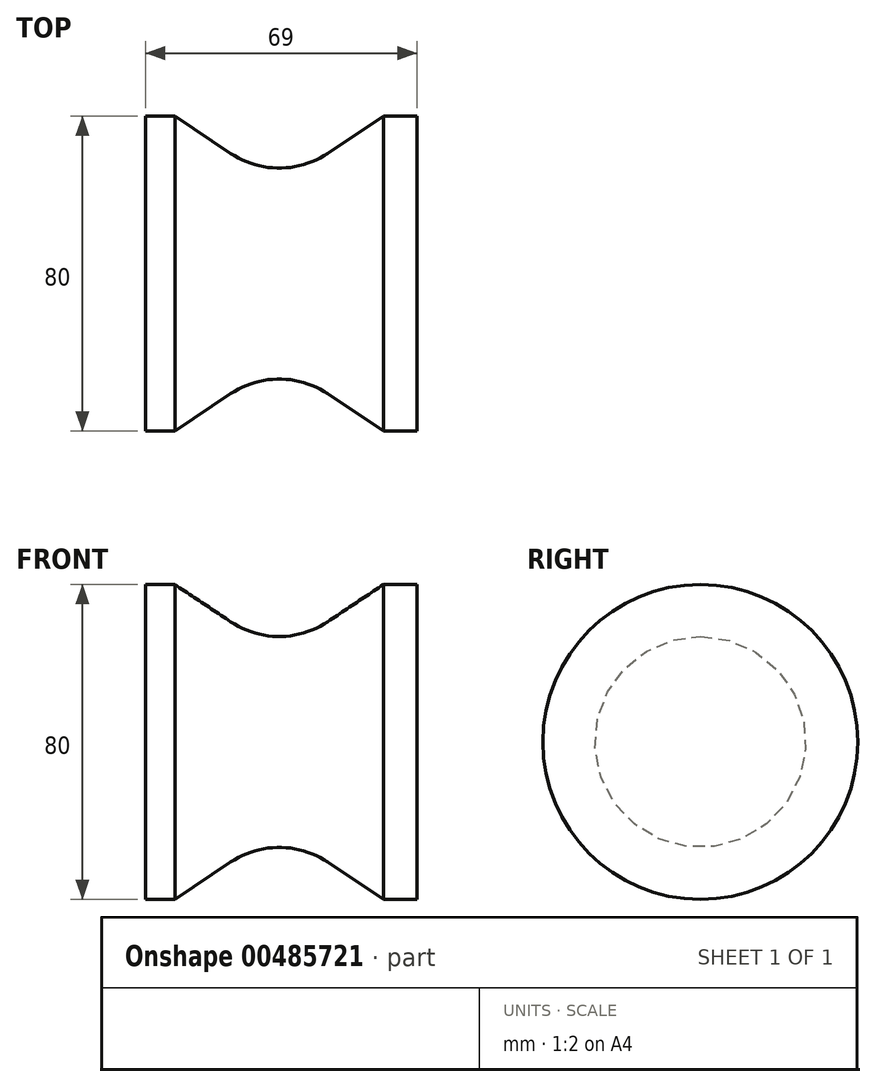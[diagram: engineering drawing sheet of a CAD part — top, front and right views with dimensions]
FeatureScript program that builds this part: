
annotation { "Feature Type Name" : "Feature", "Feature Type Description" : "" }
export const myFeature = defineFeature(function(context is Context, id is Id, definition is map)
    precondition{}
    {
        {
            var Q0;
            Q0=qCreatedBy(makeId("Front.planeOp"),FACE);
            var sketch = newSketch(context, id + "F0", { "sketchPlane" : qUnion([Q0])});
            skLineSegment(sketch, "E0.bottom", {"start": v(0, 0) * mm, "end": v(69, 0) * mm});
            skLineSegment(sketch, "E0.top", {"start": v(0, 40) * mm, "end": v(7.5, 40) * mm});
            skLineSegment(sketch, "E0.left", {"start": v(0, 0) * mm, "end": v(0, 40) * mm});
            skLineSegment(sketch, "E0.right", {"start": v(69, 0) * mm, "end": v(69, 40) * mm});
            skArc(sketch, "E1", {"start": v(21.67, 30.54) * mm, "mid": v(34, 26.8) * mm, "end": v(46.33, 30.54) * mm});
            skPoint(sketch, "E1.centerSnap0", {"position": v(34.5, 40) * mm});
            skLineSegment(sketch, "E2.trimOffspring", {"start": v(60.5, 40) * mm, "end": v(69, 40) * mm});
            skLineSegment(sketch, "E3", {"start": v(21.67, 30.54) * mm, "end": v(7.5, 40) * mm});
            skLineSegment(sketch, "E4", {"start": v(46.33, 30.54) * mm, "end": v(60.5, 40) * mm});
            skSolve(sketch);
        }
        {
            var Q0;
            Q0 = qSketchRegion(id + "F0", true);
            var Q1;
            Q1=sQuery(id+"F0.wireOp",EDGE,"E0.bottom");
            revolve(context, id + "F1", {"entities" : qUnion([Q0]), "axis" : qUnion([Q1]), "revolveType" : RevolveType.FULL});
        }
    });
